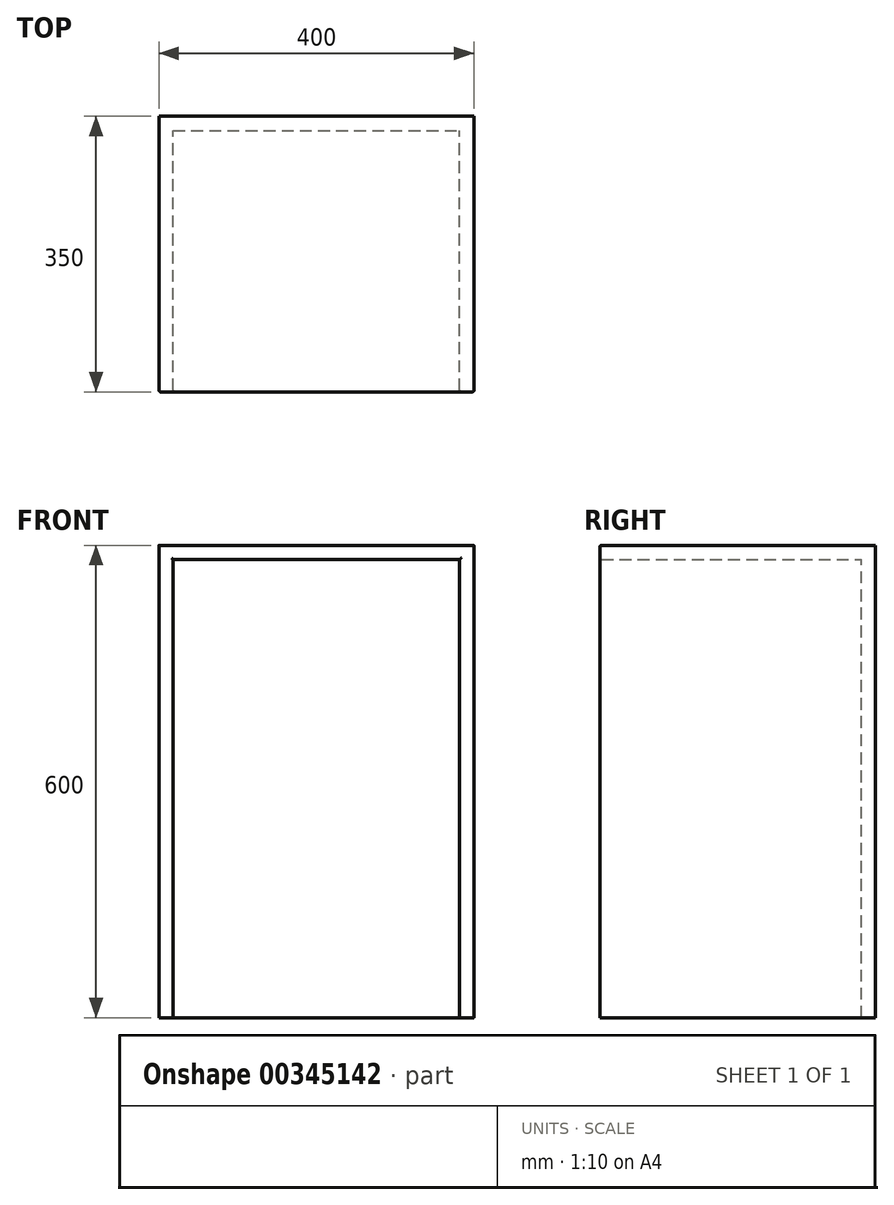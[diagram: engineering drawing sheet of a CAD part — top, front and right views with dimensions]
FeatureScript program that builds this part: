
annotation { "Feature Type Name" : "Feature", "Feature Type Description" : "" }
export const myFeature = defineFeature(function(context is Context, id is Id, definition is map)
    precondition{}
    {
        {
            var Q0;
            Q0=qCreatedBy(makeId("Front.planeOp"),FACE);
            var sketch = newSketch(context, id + "F0", { "sketchPlane" : qUnion([Q0])});
            skLineSegment(sketch, "E0.bottom", {"start": v(0, 0) * mm, "end": v(48.45, 0) * mm});
            skLineSegment(sketch, "E0.top", {"start": v(0, 45.29) * mm, "end": v(48.45, 45.29) * mm});
            skLineSegment(sketch, "E0.left", {"start": v(0, 0) * mm, "end": v(0, 45.29) * mm});
            skLineSegment(sketch, "E0.right", {"start": v(48.45, 0) * mm, "end": v(48.45, 45.29) * mm});
            skSolve(sketch);
        }
        {
            var Q0;
            Q0=makeQuery(id+"F0.imprint","IMPRINT",FACE,{"disambiguationData":[TD([[makeQuery(id+"F0.imprint","IMPRINT",EDGE,{"derivedFrom":sQuery(id+"F0.wireOp",EDGE,"E0.bottom")}),1.0]])]});
            extrude(context, id + "F1", {"entities" : qUnion([Q0]), "depth" : 350 * mm});
        }
        {
            var Q0;
            Q0=makeQuery(id+"F1.opExtrude","SWEPT_FACE",FACE,{"disambiguationData":[OSD([sQuery(id+"F0.wireOp",EDGE,"E0.left")])]});
            extrude(context, id + "F2", {"entities" : qUnion([Q0]), "operationType" : NewBodyOperationType.INTERSECT, "oppositeDirection" : true, "depth" : 18 * mm});
        }
        {
            var Q0;
            Q0=makeQuery(id+"F1.opExtrude","SWEPT_FACE",FACE,{"disambiguationData":[OSD([sQuery(id+"F0.wireOp",EDGE,"E0.bottom")])]});
            extrude(context, id + "F3", {"entities" : qUnion([Q0]), "operationType" : NewBodyOperationType.ADD, "oppositeDirection" : true, "depth" : 600 * mm});
        }
        {
            var Q0;
            {var subQ0=sQuery(id+"F0.wireOp",EDGE,"E0.left");var subQ1=sQuery(id+"F0.wireOp",EDGE,"E0.bottom");Q0=makeQuery(id+"F3.boolean.opBoolean","MERGE",FACE,{"derivedFrom":[makeQuery(id+"F1.opExtrude","SWEPT_FACE",FACE,{"disambiguationData":[OSD([subQ0])]}),makeQuery(id+"F3.opExtrude","SWEPT_FACE",FACE,{"disambiguationData":[OSD([subQ1,subQ0]),TDD([makeQuery(id+"F1.opExtrude","SWEPT_EDGE",EDGE,{"disambiguationData":[OSD([subQ1,subQ0])]})])]})]});}
            extrude(context, id + "F4", {"entities" : qUnion([Q0]), "operationType" : NewBodyOperationType.ADD, "oppositeDirection" : true, "depth" : 400 * mm});
        }
        {
            var Q0;
            {var subQ0=sQuery(id+"F0.wireOp",EDGE,"E0.left");var subQ1=sQuery(id+"F0.wireOp",EDGE,"E0.bottom");Q0=makeQuery(id+"F4.boolean.opBoolean","MERGE",FACE,{"derivedFrom":[makeQuery(id+"F3.boolean.opBoolean","MERGE",FACE,{"derivedFrom":[makeQuery(id+"F1.opExtrude","CAP_FACE",FACE,{"disambiguationData":[OSD([subQ1,sQuery(id+"F0.wireOp",EDGE,"E0.top"),subQ0,sQuery(id+"F0.wireOp",EDGE,"E0.right")])],"isStart":false}),makeQuery(id+"F3.opExtrude","SWEPT_FACE",FACE,{"disambiguationData":[OSD([subQ1]),TDD([makeQuery(id+"F1.opExtrude","CAP_EDGE",EDGE,{"disambiguationData":[OSD([subQ1])],"isStart":false})])]})]}),makeQuery(id+"F4.opExtrude","SWEPT_FACE",FACE,{"disambiguationData":[OSD([subQ1,subQ0]),TDD([makeQuery(id+"F3.boolean.opBoolean","MERGE",EDGE,{"derivedFrom":[makeQuery(id+"F1.opExtrude","CAP_EDGE",EDGE,{"disambiguationData":[OSD([subQ0])],"isStart":false}),makeQuery(id+"F3.opExtrude","SWEPT_EDGE",EDGE,{"disambiguationData":[OSD([subQ1,subQ0]),TDD([makeQuery(id+"F1.opExtrude","CAP_VERTEX",VERTEX,{"disambiguationData":[OSD([subQ1,subQ0])],"isStart":false})])]})]})])]})]});}
            var Q1;
            {var subQ0=sQuery(id+"F0.wireOp",EDGE,"E0.left");var subQ1=sQuery(id+"F0.wireOp",EDGE,"E0.bottom");Q1=makeQuery(id+"F4.boolean.opBoolean","MERGE",FACE,{"derivedFrom":[makeQuery(id+"F1.opExtrude","SWEPT_FACE",FACE,{"disambiguationData":[OSD([subQ1])]}),makeQuery(id+"F4.opExtrude","SWEPT_FACE",FACE,{"disambiguationData":[OSD([subQ1,subQ0]),TDD([makeQuery(id+"F1.opExtrude","SWEPT_EDGE",EDGE,{"disambiguationData":[OSD([subQ1,subQ0])]})])]})]});}
            shell(context, id + "F5", {"entities" : qUnion([Q0, Q1]), "thickness" : 18 * mm});
        }
        {
            var Q0;
            {var subQ0=sQuery(id+"F0.wireOp",EDGE,"E0.left");var subQ1=sQuery(id+"F0.wireOp",EDGE,"E0.bottom");Q0=makeQuery(id+"F4.opExtrude","CAP_EDGE",EDGE,{"disambiguationData":[OSD([subQ1,subQ0]),TDD([makeQuery(id+"F3.boolean.opBoolean","MERGE",EDGE,{"derivedFrom":[makeQuery(id+"F1.opExtrude","CAP_EDGE",EDGE,{"disambiguationData":[OSD([subQ0])],"isStart":false}),makeQuery(id+"F3.opExtrude","SWEPT_EDGE",EDGE,{"disambiguationData":[OSD([subQ1,subQ0]),TDD([makeQuery(id+"F1.opExtrude","CAP_VERTEX",VERTEX,{"disambiguationData":[OSD([subQ1,subQ0])],"isStart":false})])]})]})])],"isStart":false});}
            var Q1;
            {var subQ0=sQuery(id+"F0.wireOp",EDGE,"E0.left");var subQ1=sQuery(id+"F0.wireOp",EDGE,"E0.bottom");Q1=makeQuery(id+"F4.boolean.opBoolean","MERGE",EDGE,{"derivedFrom":[makeQuery(id+"F3.opExtrude","CAP_EDGE",EDGE,{"disambiguationData":[OSD([subQ1]),TDD([makeQuery(id+"F1.opExtrude","CAP_EDGE",EDGE,{"disambiguationData":[OSD([subQ1])],"isStart":false})])],"isStart":false}),makeQuery(id+"F4.opExtrude","SWEPT_EDGE",EDGE,{"disambiguationData":[OSD([subQ1,subQ0]),TDD([makeQuery(id+"F3.opExtrude","CAP_VERTEX",VERTEX,{"disambiguationData":[OSD([subQ1,subQ0]),TDD([makeQuery(id+"F1.opExtrude","CAP_VERTEX",VERTEX,{"disambiguationData":[OSD([subQ1,subQ0])],"isStart":false})])],"isStart":false})])]})]});}
            var Q2;
            {var subQ0=sQuery(id+"F0.wireOp",EDGE,"E0.left");var subQ1=sQuery(id+"F0.wireOp",EDGE,"E0.bottom");Q2=makeQuery(id+"F3.boolean.opBoolean","MERGE",EDGE,{"derivedFrom":[makeQuery(id+"F1.opExtrude","CAP_EDGE",EDGE,{"disambiguationData":[OSD([subQ0])],"isStart":false}),makeQuery(id+"F3.opExtrude","SWEPT_EDGE",EDGE,{"disambiguationData":[OSD([subQ1,subQ0]),TDD([makeQuery(id+"F1.opExtrude","CAP_VERTEX",VERTEX,{"disambiguationData":[OSD([subQ1,subQ0])],"isStart":false})])]})]});}
            fillet(context, id + "F6", {"entities" : qUnion([Q0, Q1, Q2]), "radius" : 2 * mm, "tangentPropagation" : true, "allowEdgeOverflow" : false});
        }
        {
            var Q0;
            {var subQ0=sQuery(id+"F0.wireOp",EDGE,"E0.left");var subQ1=sQuery(id+"F0.wireOp",EDGE,"E0.bottom");Q0=makeQuery(id+"F5.opShell","OFFSET_EDGE",EDGE,{"disambiguationData":[OSD([subQ1,subQ0]),TDD([makeQuery(id+"F3.boolean.opBoolean","MERGE",EDGE,{"derivedFrom":[makeQuery(id+"F1.opExtrude","CAP_EDGE",EDGE,{"disambiguationData":[OSD([subQ0])],"isStart":false}),makeQuery(id+"F3.opExtrude","SWEPT_EDGE",EDGE,{"disambiguationData":[OSD([subQ1,subQ0]),TDD([makeQuery(id+"F1.opExtrude","CAP_VERTEX",VERTEX,{"disambiguationData":[OSD([subQ1,subQ0])],"isStart":false})])]})]})])]});}
            var Q1;
            {var subQ0=sQuery(id+"F0.wireOp",EDGE,"E0.left");var subQ1=sQuery(id+"F0.wireOp",EDGE,"E0.bottom");Q1=makeQuery(id+"F5.opShell","OFFSET_EDGE",EDGE,{"disambiguationData":[OSD([subQ1,subQ0]),TDD([makeQuery(id+"F4.opExtrude","CAP_EDGE",EDGE,{"disambiguationData":[OSD([subQ1,subQ0]),TDD([makeQuery(id+"F3.boolean.opBoolean","MERGE",EDGE,{"derivedFrom":[makeQuery(id+"F1.opExtrude","CAP_EDGE",EDGE,{"disambiguationData":[OSD([subQ0])],"isStart":false}),makeQuery(id+"F3.opExtrude","SWEPT_EDGE",EDGE,{"disambiguationData":[OSD([subQ1,subQ0]),TDD([makeQuery(id+"F1.opExtrude","CAP_VERTEX",VERTEX,{"disambiguationData":[OSD([subQ1,subQ0])],"isStart":false})])]})]})])],"isStart":false})])]});}
            var Q2;
            {var subQ0=sQuery(id+"F0.wireOp",EDGE,"E0.left");var subQ1=sQuery(id+"F0.wireOp",EDGE,"E0.bottom");Q2=makeQuery(id+"F5.opShell","OFFSET_EDGE",EDGE,{"disambiguationData":[OSD([subQ1,subQ0]),TDD([makeQuery(id+"F4.boolean.opBoolean","MERGE",EDGE,{"derivedFrom":[makeQuery(id+"F3.opExtrude","CAP_EDGE",EDGE,{"disambiguationData":[OSD([subQ1]),TDD([makeQuery(id+"F1.opExtrude","CAP_EDGE",EDGE,{"disambiguationData":[OSD([subQ1])],"isStart":false})])],"isStart":false}),makeQuery(id+"F4.opExtrude","SWEPT_EDGE",EDGE,{"disambiguationData":[OSD([subQ1,subQ0]),TDD([makeQuery(id+"F3.opExtrude","CAP_VERTEX",VERTEX,{"disambiguationData":[OSD([subQ1,subQ0]),TDD([makeQuery(id+"F1.opExtrude","CAP_VERTEX",VERTEX,{"disambiguationData":[OSD([subQ1,subQ0])],"isStart":false})])],"isStart":false})])]})]})])]});}
            fillet(context, id + "F7", {"entities" : qUnion([Q0, Q1, Q2]), "radius" : 2 * mm, "tangentPropagation" : true, "allowEdgeOverflow" : false});
        }
    });
